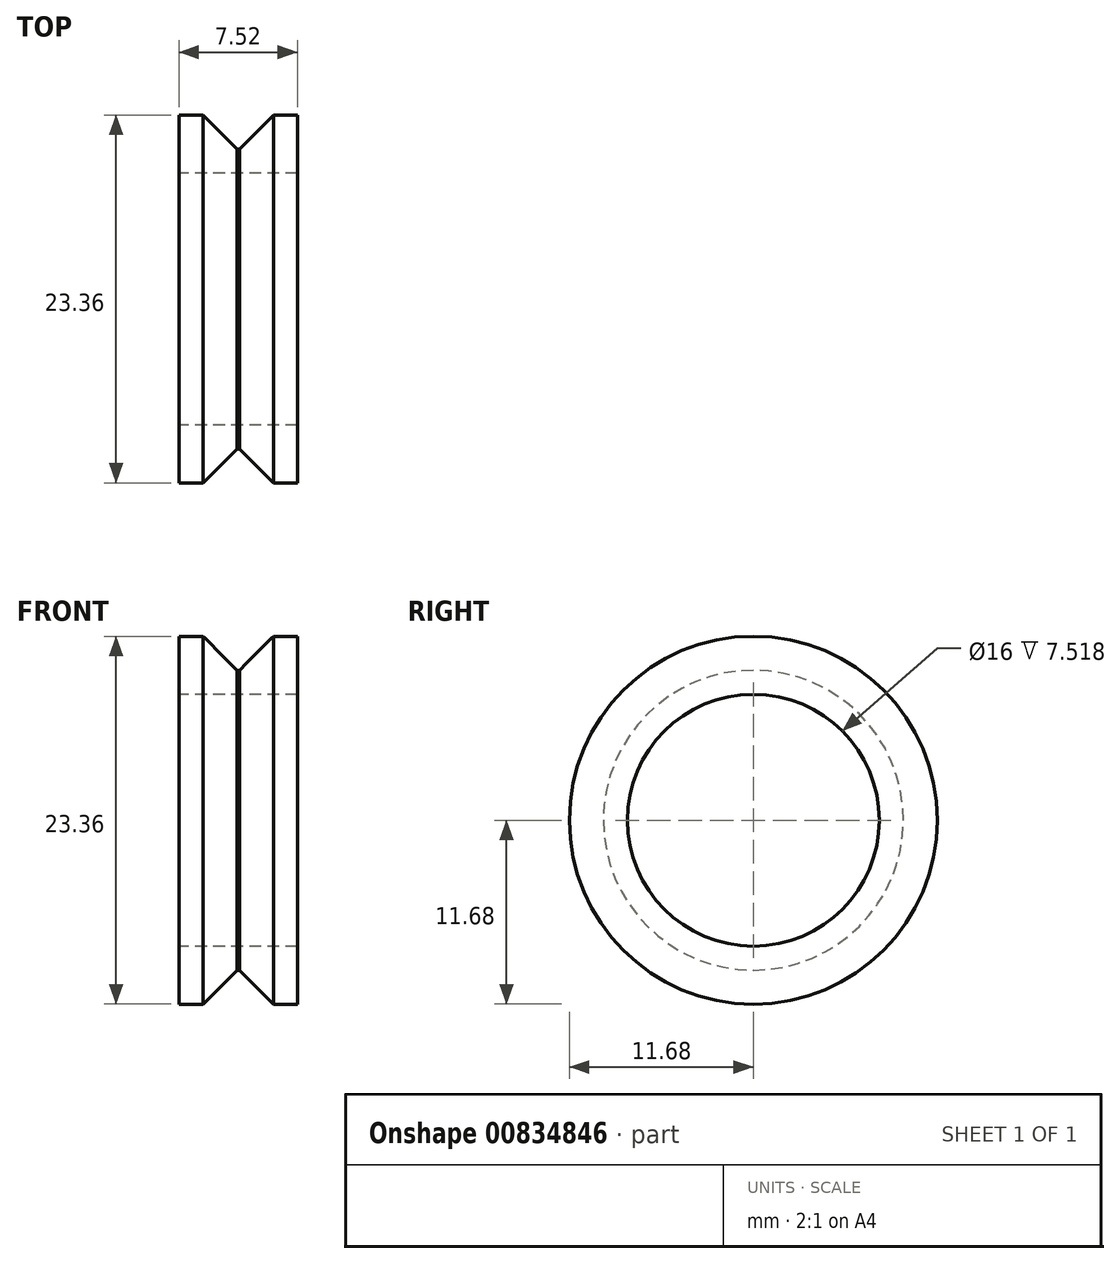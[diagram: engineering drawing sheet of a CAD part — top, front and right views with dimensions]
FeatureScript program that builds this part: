
annotation { "Feature Type Name" : "Feature", "Feature Type Description" : "" }
export const myFeature = defineFeature(function(context is Context, id is Id, definition is map)
    precondition{}
    {
        {
            var Q0;
            Q0=qCreatedBy(makeId("Front.planeOp"),FACE);
            var sketch = newSketch(context, id + "F0", { "sketchPlane" : qUnion([Q0])});
            skLineSegment(sketch, "E0", {"start": v(-3.76, 11.68) * mm, "end": v(-3.76, 8) * mm});
            skLineSegment(sketch, "E1", {"start": v(-3.76, 8) * mm, "end": v(0, 8) * mm});
            skLineSegment(sketch, "E2", {"start": v(0, 9.53) * mm, "end": v(-0.08, 9.53) * mm});
            skLineSegment(sketch, "E3", {"start": v(-0.08, 9.53) * mm, "end": v(-2.24, 11.68) * mm});
            skLineSegment(sketch, "E4", {"start": v(-2.24, 11.68) * mm, "end": v(-3.76, 11.68) * mm});
            skLineSegment(sketch, "E5", {"start": v(-7.12, 0) * mm, "end": v(9.17, 0) * mm, "construction": true});
            skLineSegment(sketch, "E6", {"start": v(0, 16.15) * mm, "end": v(0, 0) * mm, "construction": true});
            skLineSegment(sketch, "E7.MirrorCS", {"start": v(0, 9.53) * mm, "end": v(0.08, 9.53) * mm});
            skLineSegment(sketch, "E8.MirrorCS", {"start": v(2.24, 11.68) * mm, "end": v(3.76, 11.68) * mm});
            skLineSegment(sketch, "E9.MirrorCS", {"start": v(0.08, 9.53) * mm, "end": v(2.24, 11.68) * mm});
            skLineSegment(sketch, "E10.MirrorCS", {"start": v(3.76, 8) * mm, "end": v(0, 8) * mm});
            skLineSegment(sketch, "E11.MirrorCS", {"start": v(3.76, 11.68) * mm, "end": v(3.76, 8) * mm});
            skSolve(sketch);
        }
        {
            var Q0;
            Q0=makeQuery(id+"F0.imprint","IMPRINT",FACE,{"disambiguationData":[TD([[makeQuery(id+"F0.imprint","IMPRINT",EDGE,{"derivedFrom":sQuery(id+"F0.wireOp",EDGE,"E0")}),1.0]])]});
            var Q1;
            Q1=sQuery(id+"F0.wireOp",EDGE,"E5");
            revolve(context, id + "F1", {"entities" : qUnion([Q0]), "axis" : qUnion([Q1]), "revolveType" : RevolveType.FULL});
        }
    });
